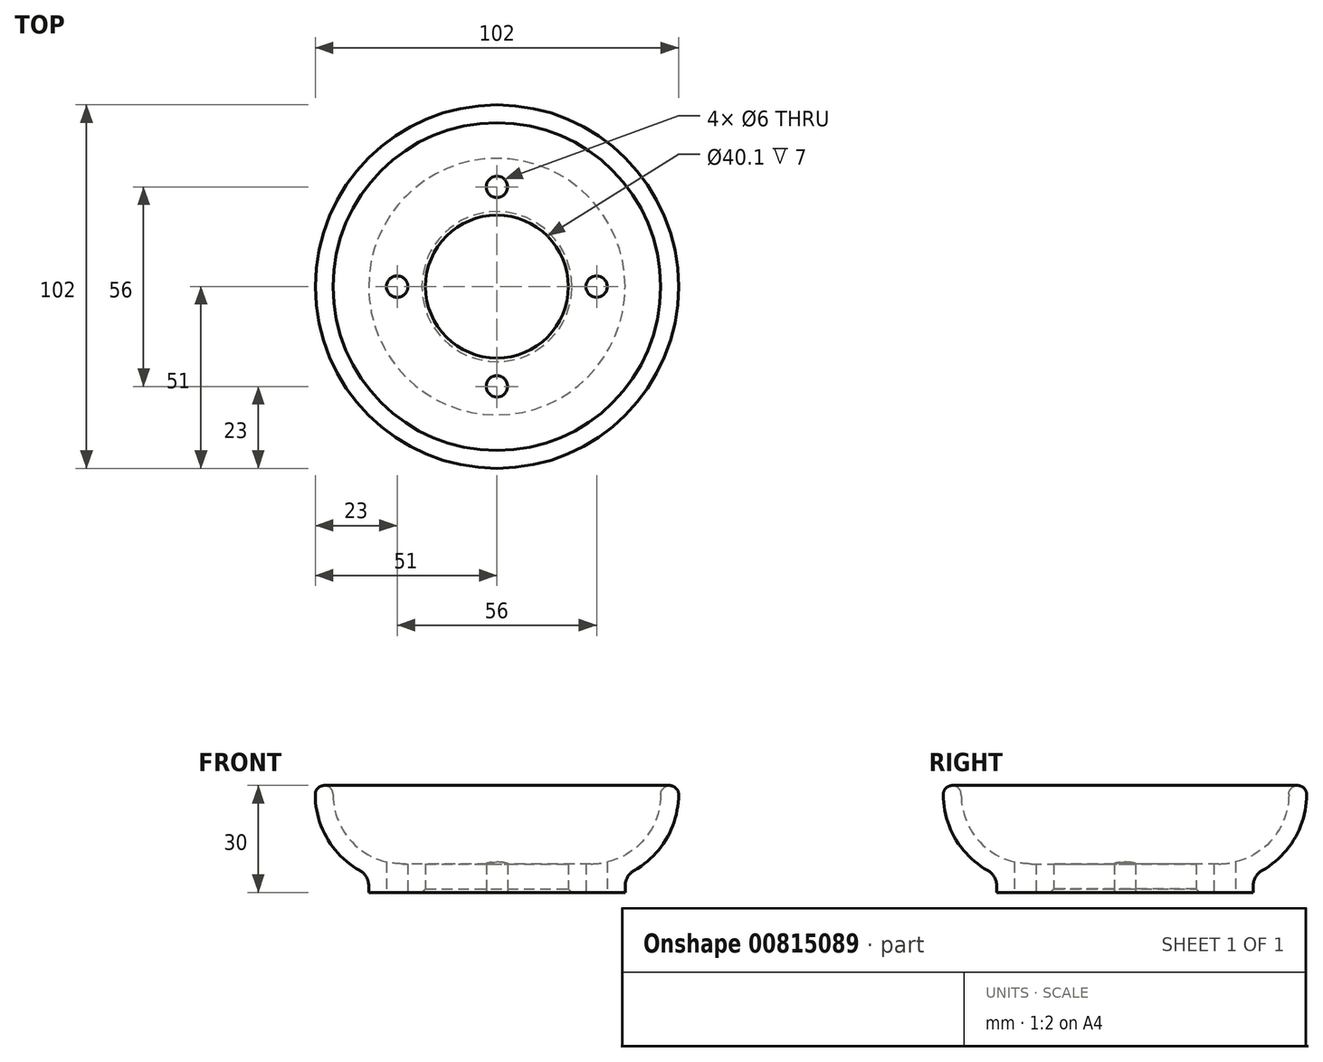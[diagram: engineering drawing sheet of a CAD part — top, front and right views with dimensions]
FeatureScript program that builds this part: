
annotation { "Feature Type Name" : "Feature", "Feature Type Description" : "" }
export const myFeature = defineFeature(function(context is Context, id is Id, definition is map)
    precondition{}
    {
        {
            var Q0;
            Q0=qCreatedBy(makeId("Front.planeOp"),FACE);
            var sketch = newSketch(context, id + "F0", { "sketchPlane" : qUnion([Q0])});
            skLineSegment(sketch, "E0", {"start": v(-20.05, 0) * mm, "end": v(-36, 0) * mm});
            skLineSegment(sketch, "E1", {"start": v(0, 0) * mm, "end": v(0, 8) * mm});
            skLineSegment(sketch, "E2", {"start": v(-20.05, 8) * mm, "end": v(-26.5, 8) * mm});
            skLineSegment(sketch, "E3", {"start": v(-20.05, 8) * mm, "end": v(-20.05, 0) * mm});
            skArc(sketch, "E4", {"start": v(-46, 27.5) * mm, "mid": v(-40.29, 13.71) * mm, "end": v(-26.5, 8) * mm});
            skArc(sketch, "E5", {"start": v(-46, 27.5) * mm, "mid": v(-48.5, 30) * mm, "end": v(-51, 27.5) * mm});
            skArc(sketch, "E6", {"start": v(-51, 27.5) * mm, "mid": v(-47.66, 15.15) * mm, "end": v(-38.54, 6.16) * mm});
            skLineSegment(sketch, "E7", {"start": v(-36, 0) * mm, "end": v(-36, 1.8) * mm});
            skArc(sketch, "E8.filletArc", {"start": v(-36, 1.8) * mm, "mid": v(-36.68, 4.33) * mm, "end": v(-38.54, 6.16) * mm});
            skSolve(sketch);
        }
        {
            var Q0;
            Q0 = qSketchRegion(id + "F0", true);
            var Q1;
            Q1=sQuery(id+"F0.wireOp",EDGE,"E1");
            revolve(context, id + "F1", {"surfaceOperationType" : NewSurfaceOperationType.NEW, "entities" : qUnion([Q0]), "axis" : qUnion([Q1]), "revolveType" : RevolveType.FULL});
        }
        {
            var Q0;
            Q0=makeQuery(id+"F1.opRevolve","SWEPT_EDGE",EDGE,{"disambiguationData":[OSD([sQuery(id+"F0.wireOp",EDGE,"E0"),sQuery(id+"F0.wireOp",EDGE,"E3")])]});
            chamfer(context, id + "F2", {"entities" : qUnion([Q0]), "width" : 1 * mm, "tangentPropagation" : true});
        }
        {
            var Q0;
            Q0=qCreatedBy(makeId("Top.planeOp"),FACE);
            var sketch = newSketch(context, id + "F3", { "sketchPlane" : qUnion([Q0])});
            skCircle(sketch, "E9", {"center": v(-28, 0) * mm, "radius": 3 * mm});
            skCircle(sketch, "E10", {"center": v(0, 28) * mm, "radius": 3 * mm});
            skCircle(sketch, "E11", {"center": v(28, 0) * mm, "radius": 3 * mm});
            skCircle(sketch, "E12", {"center": v(0, -28) * mm, "radius": 3 * mm});
            skSolve(sketch);
        }
        {
            var Q0;
            Q0 = qSketchRegion(id + "F3", true);
            extrude(context, id + "F4", {"entities" : qUnion([Q0]), "operationType" : NewBodyOperationType.REMOVE, "depth" : 25 * mm, "offsetDistance" : 25 * mm});
        }
    });
